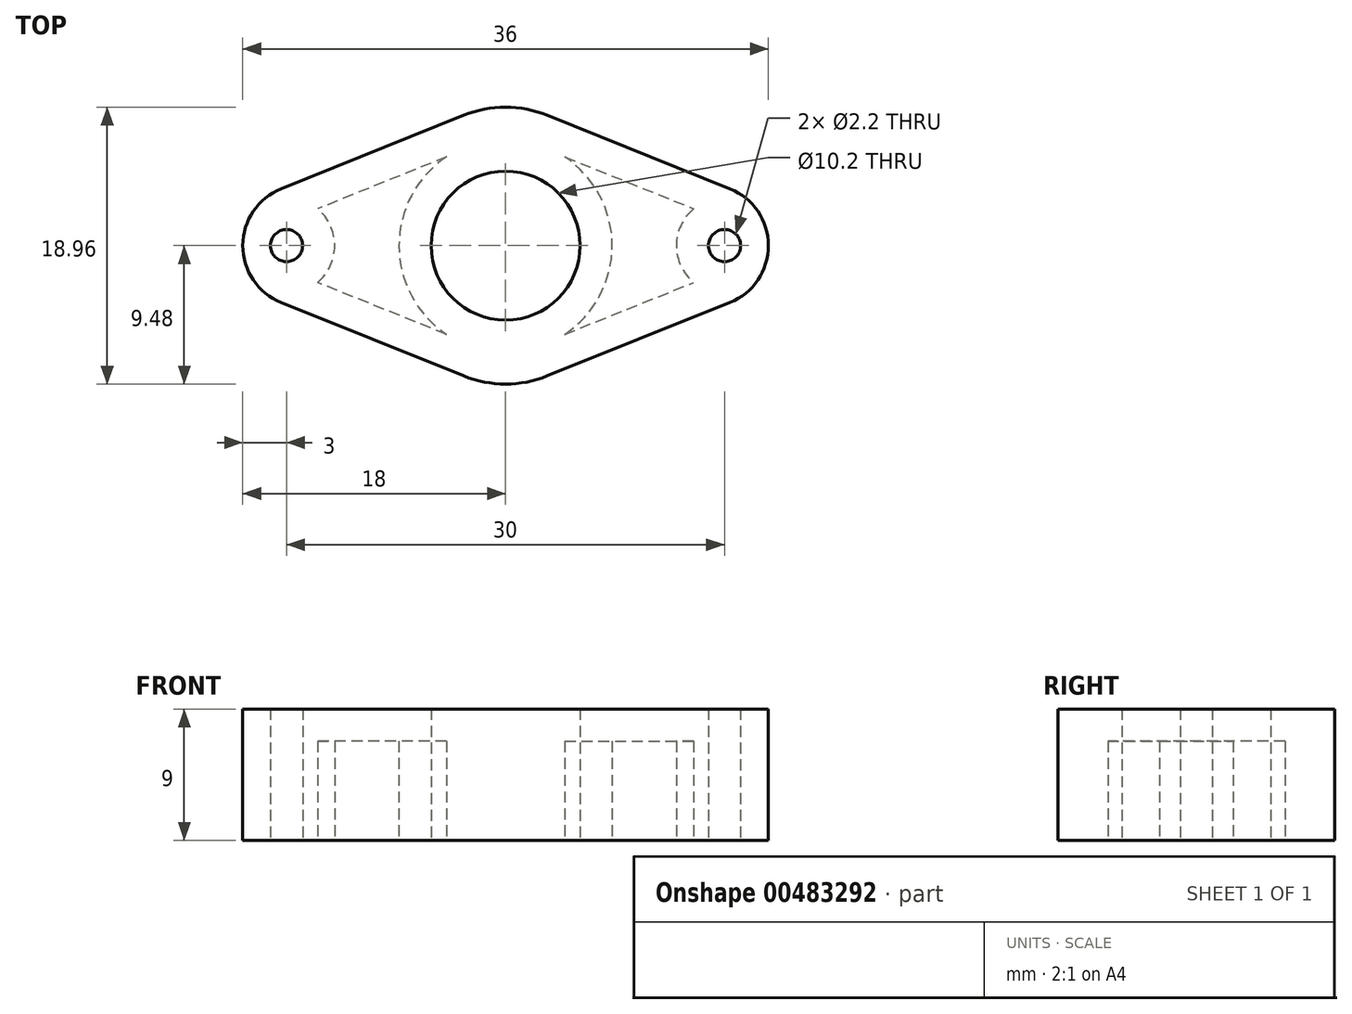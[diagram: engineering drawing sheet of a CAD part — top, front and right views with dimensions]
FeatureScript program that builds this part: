
annotation { "Feature Type Name" : "Feature", "Feature Type Description" : "" }
export const myFeature = defineFeature(function(context is Context, id is Id, definition is map)
    precondition{}
    {
        {
            var Q0;
            Q0=qCreatedBy(makeId("Top.planeOp"),FACE);
            var sketch = newSketch(context, id + "F0", { "sketchPlane" : qUnion([Q0])});
            skCircle(sketch, "E0", {"center": v(0, 0) * mm, "radius": 5.1 * mm});
            skCircle(sketch, "E1", {"center": v(-15, 0) * mm, "radius": 1.1 * mm});
            skLineSegment(sketch, "E2", {"start": v(-2.86, 8.92) * mm, "end": v(-15.37, 3.9) * mm});
            skArc(sketch, "E3", {"start": v(-15.37, 3.9) * mm, "mid": v(-17.28, 2.35) * mm, "end": v(-18, 0) * mm});
            skArc(sketch, "E4", {"start": v(0, 9.48) * mm, "mid": v(-1.46, 9.34) * mm, "end": v(-2.86, 8.92) * mm});
            skCircle(sketch, "E5.MirrorC", {"center": v(15, 0) * mm, "radius": 1.1 * mm});
            skLineSegment(sketch, "E6.MirrorCS", {"start": v(2.86, 8.92) * mm, "end": v(15.37, 3.9) * mm});
            skArc(sketch, "E7.MirrorCS", {"start": v(15.37, 3.9) * mm, "mid": v(17.28, 2.35) * mm, "end": v(18, 0) * mm});
            skArc(sketch, "E8.MirrorCS", {"start": v(0, 9.48) * mm, "mid": v(1.46, 9.34) * mm, "end": v(2.86, 8.92) * mm});
            skArc(sketch, "E9.MirrorCS", {"start": v(0, -9.48) * mm, "mid": v(-1.46, -9.34) * mm, "end": v(-2.86, -8.92) * mm});
            skArc(sketch, "E10.MirrorCS", {"start": v(-15.37, -3.9) * mm, "mid": v(-17.28, -2.35) * mm, "end": v(-18, 0) * mm});
            skLineSegment(sketch, "E11.MirrorCS", {"start": v(-2.86, -8.92) * mm, "end": v(-15.37, -3.9) * mm});
            skLineSegment(sketch, "E12.MirrorCS", {"start": v(2.86, -8.92) * mm, "end": v(15.37, -3.9) * mm});
            skArc(sketch, "E13.MirrorCS", {"start": v(15.37, -3.9) * mm, "mid": v(17.28, -2.35) * mm, "end": v(18, 0) * mm});
            skArc(sketch, "E14.MirrorCS", {"start": v(0, -9.48) * mm, "mid": v(1.46, -9.34) * mm, "end": v(2.86, -8.92) * mm});
            skSolve(sketch);
        }
        {
            var Q0;
            Q0=makeQuery(id+"F0.imprint","IMPRINT",FACE,{"disambiguationData":[TD([[makeQuery(id+"F0.imprint","IMPRINT",EDGE,{"derivedFrom":sQuery(id+"F0.wireOp",EDGE,"E2")}),1.0]])]});
            extrude(context, id + "F1", {"entities" : qUnion([Q0]), "depth" : 9 * mm});
        }
        {
            var Q0;
            Q0=makeQuery(id+"F1.opExtrude","CAP_FACE",FACE,{"disambiguationData":[OSD([sQuery(id+"F0.wireOp",EDGE,"E2"),sQuery(id+"F0.wireOp",EDGE,"E3"),sQuery(id+"F0.wireOp",EDGE,"E4"),sQuery(id+"F0.wireOp",EDGE,"E6.MirrorCS"),sQuery(id+"F0.wireOp",EDGE,"E7.MirrorCS"),sQuery(id+"F0.wireOp",EDGE,"E8.MirrorCS"),sQuery(id+"F0.wireOp",EDGE,"E5.MirrorC"),sQuery(id+"F0.wireOp",EDGE,"E0"),sQuery(id+"F0.wireOp",EDGE,"E9.MirrorCS"),sQuery(id+"F0.wireOp",EDGE,"E10.MirrorCS"),sQuery(id+"F0.wireOp",EDGE,"E11.MirrorCS"),sQuery(id+"F0.wireOp",EDGE,"E12.MirrorCS"),sQuery(id+"F0.wireOp",EDGE,"E13.MirrorCS"),sQuery(id+"F0.wireOp",EDGE,"E1"),sQuery(id+"F0.wireOp",EDGE,"E14.MirrorCS")])],"isStart":true});
            shell(context, id + "F2", {"entities" : qUnion([Q0]), "thickness" : 2.2 * mm});
        }
    });
